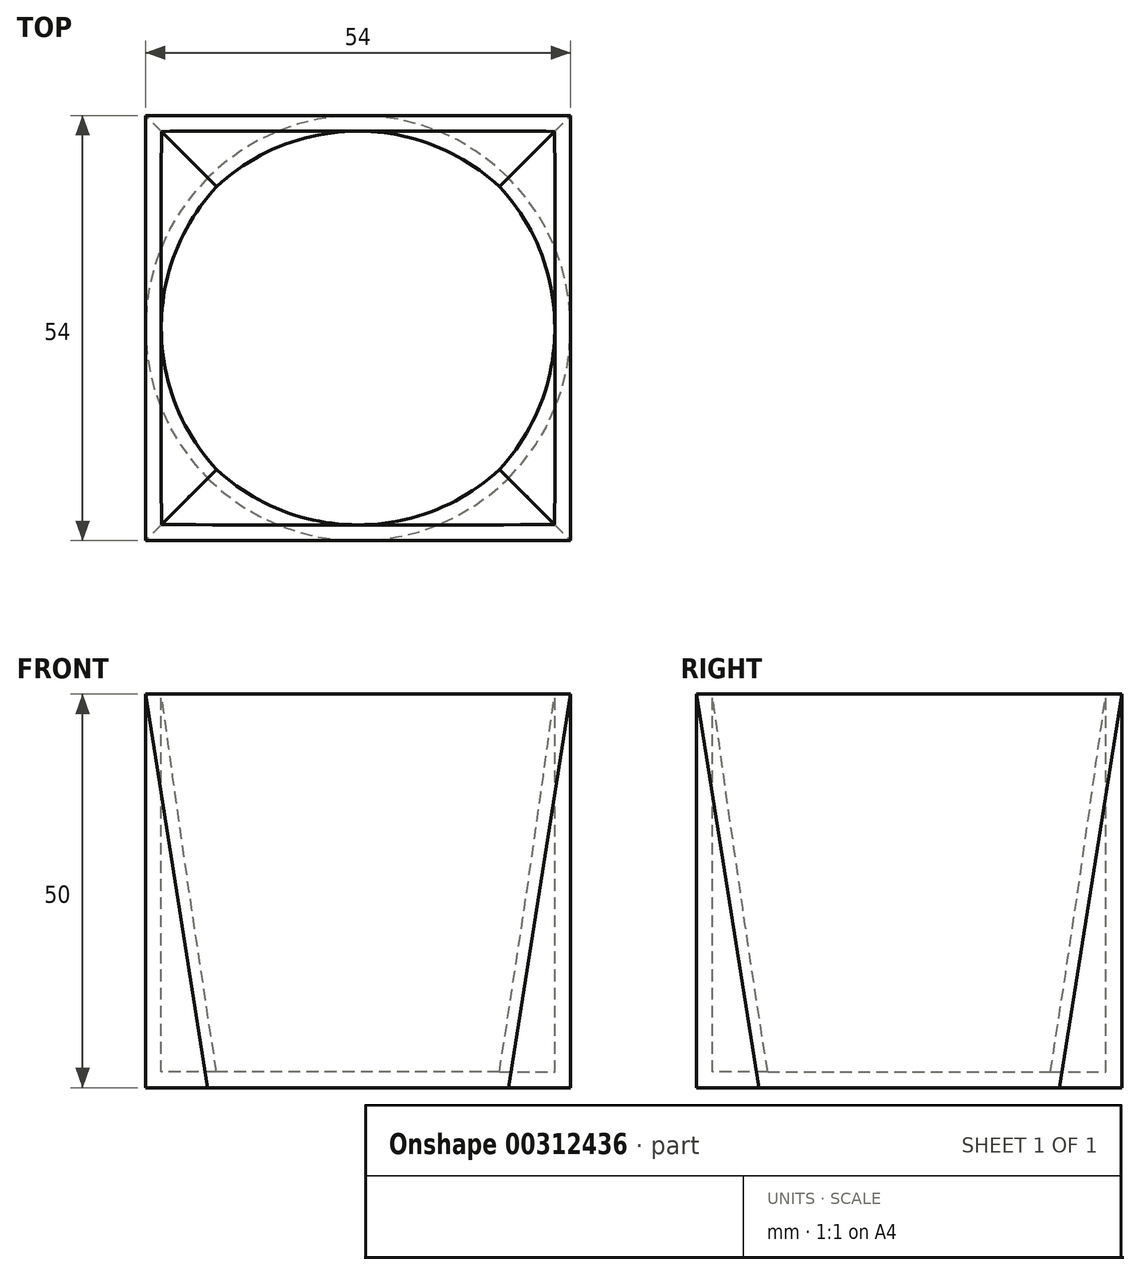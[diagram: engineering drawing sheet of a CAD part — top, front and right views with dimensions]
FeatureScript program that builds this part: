
annotation { "Feature Type Name" : "Feature", "Feature Type Description" : "" }
export const myFeature = defineFeature(function(context is Context, id is Id, definition is map)
    precondition{}
    {
        {
            var Q0;
            Q0=qCreatedBy(makeId("Top.planeOp"),FACE);
            var sketch = newSketch(context, id + "F0", { "sketchPlane" : qUnion([Q0])});
            skCircle(sketch, "E0", {"center": v(0, 0) * mm, "radius": 27 * mm});
            skSolve(sketch);
        }
        {
            var Q0;
            Q0=qCreatedBy(makeId("Top.planeOp"),FACE);
            cPlane(context, id + "F1", {"entities" : qUnion([Q0]), "cplaneType" : CPlaneType.OFFSET, "offset" : 50 * mm, "width" : 150 * mm, "height" : 150 * mm});
        }
        {
            var Q0;
            Q0=qCreatedBy(id+"F1.planeOp",FACE);
            var sketch = newSketch(context, id + "F2", { "sketchPlane" : qUnion([Q0])});
            skPoint(sketch, "E1.middle", {"position": v(0, 0) * mm});
            skPoint(sketch, "E1.left.start.orphan", {"position": v(-18.6, 18.6) * mm});
            skPoint(sketch, "E1.right.start.orphan", {"position": v(18.6, 18.6) * mm});
            skPoint(sketch, "E1.top.end.orphan", {"position": v(18.6, -18.6) * mm});
            skPoint(sketch, "E1.top.start.orphan", {"position": v(-18.6, -18.6) * mm});
            skLineSegment(sketch, "E2.bottom", {"start": v(-27, 27) * mm, "end": v(27, 27) * mm});
            skLineSegment(sketch, "E2.top", {"start": v(-27, -27) * mm, "end": v(27, -27) * mm});
            skLineSegment(sketch, "E2.left", {"start": v(-27, 27) * mm, "end": v(-27, -27) * mm});
            skLineSegment(sketch, "E2.right", {"start": v(27, 27) * mm, "end": v(27, -27) * mm});
            skSolve(sketch);
        }
        {
            var Q0;
            Q0=makeQuery(id+"F0.imprint","IMPRINT",FACE,{"disambiguationData":[TD([[makeQuery(id+"F0.imprint","IMPRINT",EDGE,{"derivedFrom":sQuery(id+"F0.wireOp",EDGE,"E0")}),1.0]])]});
            var Q1;
            Q1=makeQuery(id+"F2.imprint","IMPRINT",FACE,{"disambiguationData":[TD([[makeQuery(id+"F2.imprint","IMPRINT",EDGE,{"derivedFrom":sQuery(id+"F2.wireOp",EDGE,"E2.bottom")}),-1.0]])]});
            loft(context, id + "F3", {"sheetProfilesArray" : [{ "sheetProfileEntities" : qUnion([Q0]) }, { "sheetProfileEntities" : qUnion([Q1]) }]});
        }
        {
            var Q0;
            Q0=makeQuery(id+"F3.opLoft","CAP_FACE",FACE,{"disambiguationData":[OSD([makeQuery(id+"F2.imprint","IMPRINT",FACE,{"disambiguationData":[TD([[makeQuery(id+"F2.imprint","IMPRINT",EDGE,{"derivedFrom":sQuery(id+"F2.wireOp",EDGE,"E2.bottom")}),-1.0]])]})])],"isStart":true});
            shell(context, id + "F4", {"entities" : qUnion([Q0]), "thickness" : 2 * mm});
        }
    });
